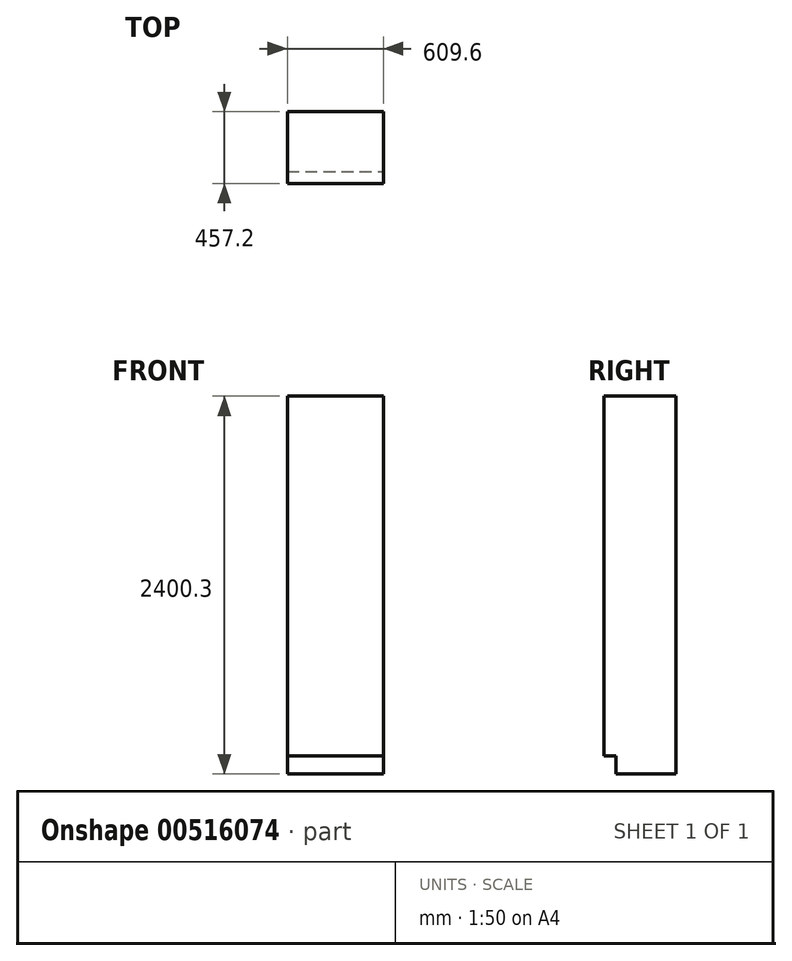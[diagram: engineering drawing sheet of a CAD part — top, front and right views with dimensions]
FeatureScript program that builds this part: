
annotation { "Feature Type Name" : "Feature", "Feature Type Description" : "" }
export const myFeature = defineFeature(function(context is Context, id is Id, definition is map)
    precondition{}
    {
        {
            var Q0;
            Q0=qCreatedBy(makeId("Top.planeOp"),FACE);
            var sketch = newSketch(context, id + "F0", { "sketchPlane" : qUnion([Q0])});
            skLineSegment(sketch, "E0.bottom", {"start": v(304.8, -228.6) * mm, "end": v(-304.8, -228.6) * mm});
            skLineSegment(sketch, "E0.top", {"start": v(304.8, 228.6) * mm, "end": v(-304.8, 228.6) * mm});
            skLineSegment(sketch, "E0.left", {"start": v(304.8, -228.6) * mm, "end": v(304.8, 228.6) * mm});
            skLineSegment(sketch, "E0.right", {"start": v(-304.8, -228.6) * mm, "end": v(-304.8, 228.6) * mm});
            skPoint(sketch, "E0.middle", {"position": v(0, 0) * mm});
            skLineSegment(sketch, "E1", {"start": v(-304.8, -152.4) * mm, "end": v(304.8, -152.4) * mm});
            skSolve(sketch);
        }
        {
            var Q0;
            {var subQ0=sQuery(id+"F0.wireOp",EDGE,"E0.top");Q0=makeQuery(id+"F0.imprint","IMPRINT",FACE,{"disambiguationData":[TD([[makeQuery(id+"F0.imprint","IMPRINT",EDGE,{"derivedFrom":subQ0}),1.0]])]});}
            var Q1;
            {var subQ0=sQuery(id+"F0.wireOp",EDGE,"E0.bottom");Q1=makeQuery(id+"F0.imprint","IMPRINT",FACE,{"disambiguationData":[TD([[makeQuery(id+"F0.imprint","IMPRINT",EDGE,{"derivedFrom":subQ0}),-1.0]])]});}
            extrude(context, id + "F1", {"entities" : qUnion([Q0, Q1]), "depth" : 2286 * mm, "offsetDistance" : 25.4 * mm});
        }
        {
            var Q0;
            {var subQ0=sQuery(id+"F0.wireOp",EDGE,"E0.top");Q0=makeQuery(id+"F0.imprint","IMPRINT",FACE,{"disambiguationData":[TD([[makeQuery(id+"F0.imprint","IMPRINT",EDGE,{"derivedFrom":subQ0}),1.0]])]});}
            extrude(context, id + "F2", {"entities" : qUnion([Q0]), "operationType" : NewBodyOperationType.ADD, "oppositeDirection" : true, "depth" : 114.3 * mm, "offsetDistance" : 25.4 * mm});
        }
    });
